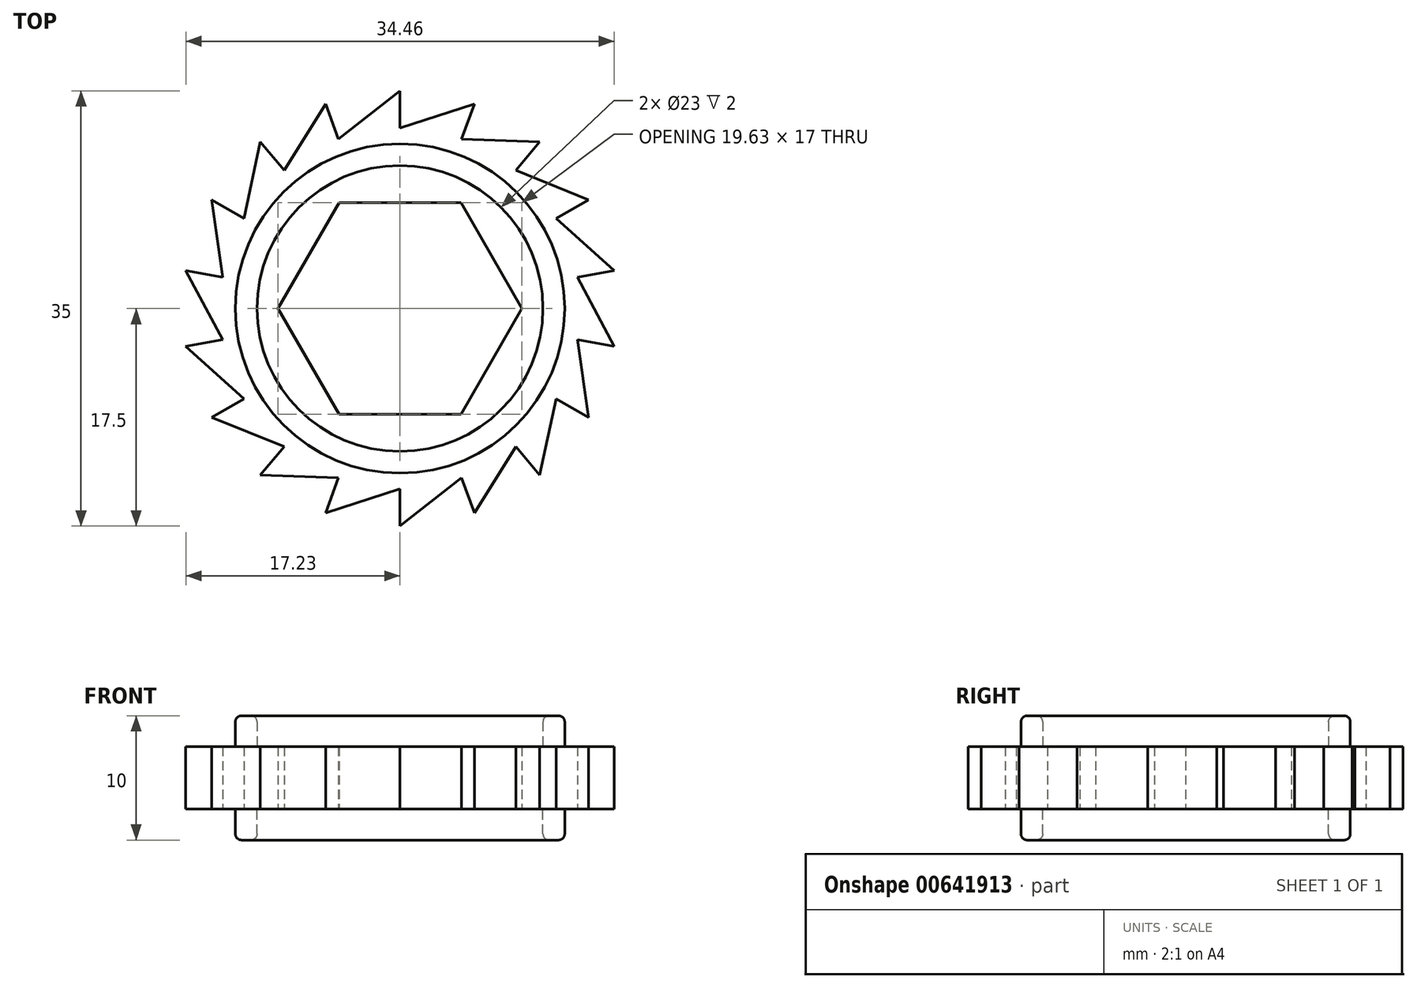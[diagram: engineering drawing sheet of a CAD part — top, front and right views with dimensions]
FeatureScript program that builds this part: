
annotation { "Feature Type Name" : "Feature", "Feature Type Description" : "" }
export const myFeature = defineFeature(function(context is Context, id is Id, definition is map)
    precondition{}
    {
        {
            var Q0;
            Q0=qCreatedBy(makeId("Top.planeOp"),FACE);
            var sketch = newSketch(context, id + "F0", { "sketchPlane" : qUnion([Q0])});
            skCircle(sketch, "E0", {"center": v(0, 0) * mm, "radius": 14.5 * mm});
            skCircle(sketch, "E1", {"center": v(0, 0) * mm, "radius": 17.5 * mm});
            skLineSegment(sketch, "E2", {"start": v(0, 0) * mm, "end": v(0, 17.5) * mm});
            skLineSegment(sketch, "E3.1.0", {"start": v(0, 0) * mm, "end": v(-5.99, 16.44) * mm});
            skLineSegment(sketch, "E3.2.0", {"start": v(0, 0) * mm, "end": v(-11.25, 13.4) * mm});
            skLineSegment(sketch, "E3.3.0", {"start": v(0, 0) * mm, "end": v(-15.16, 8.75) * mm});
            skLineSegment(sketch, "E3.4.0", {"start": v(0, 0) * mm, "end": v(-17.23, 3.04) * mm});
            skLineSegment(sketch, "E3.5.0", {"start": v(0, 0) * mm, "end": v(-17.23, -3.04) * mm});
            skLineSegment(sketch, "E3.6.0", {"start": v(0, 0) * mm, "end": v(-15.16, -8.75) * mm});
            skLineSegment(sketch, "E3.7.0", {"start": v(0, 0) * mm, "end": v(-11.25, -13.4) * mm});
            skLineSegment(sketch, "E3.8.0", {"start": v(0, 0) * mm, "end": v(-5.99, -16.44) * mm});
            skLineSegment(sketch, "E3.9.0", {"start": v(0, 0) * mm, "end": v(0, -17.5) * mm});
            skLineSegment(sketch, "E3.10.0", {"start": v(0, 0) * mm, "end": v(5.99, -16.44) * mm});
            skLineSegment(sketch, "E3.11.0", {"start": v(0, 0) * mm, "end": v(11.25, -13.4) * mm});
            skLineSegment(sketch, "E3.12.0", {"start": v(0, 0) * mm, "end": v(15.16, -8.75) * mm});
            skLineSegment(sketch, "E3.13.0", {"start": v(0, 0) * mm, "end": v(17.23, -3.04) * mm});
            skLineSegment(sketch, "E3.14.0", {"start": v(0, 0) * mm, "end": v(17.23, 3.04) * mm});
            skLineSegment(sketch, "E3.15.0", {"start": v(0, 0) * mm, "end": v(15.16, 8.75) * mm});
            skLineSegment(sketch, "E3.16.0", {"start": v(0, 0) * mm, "end": v(11.25, 13.4) * mm});
            skLineSegment(sketch, "E3.17.0", {"start": v(0, 0) * mm, "end": v(5.99, 16.44) * mm});
            skLineSegment(sketch, "E4", {"start": v(5.99, 16.44) * mm, "end": v(0, 14.5) * mm});
            skLineSegment(sketch, "E5.1.0", {"start": v(0, 17.5) * mm, "end": v(-4.96, 13.63) * mm});
            skLineSegment(sketch, "E5.2.0", {"start": v(-5.99, 16.44) * mm, "end": v(-9.32, 11.1) * mm});
            skLineSegment(sketch, "E5.3.0", {"start": v(-11.25, 13.4) * mm, "end": v(-12.56, 7.25) * mm});
            skLineSegment(sketch, "E5.4.0", {"start": v(-15.16, 8.75) * mm, "end": v(-14.28, 2.52) * mm});
            skLineSegment(sketch, "E5.5.0", {"start": v(-17.23, 3.04) * mm, "end": v(-14.28, -2.52) * mm});
            skLineSegment(sketch, "E5.6.0", {"start": v(-17.23, -3.04) * mm, "end": v(-12.56, -7.25) * mm});
            skLineSegment(sketch, "E5.7.0", {"start": v(-15.16, -8.75) * mm, "end": v(-9.32, -11.1) * mm});
            skLineSegment(sketch, "E5.8.0", {"start": v(-11.25, -13.4) * mm, "end": v(-4.96, -13.63) * mm});
            skLineSegment(sketch, "E5.9.0", {"start": v(-5.99, -16.44) * mm, "end": v(0, -14.5) * mm});
            skLineSegment(sketch, "E5.10.0", {"start": v(0, -17.5) * mm, "end": v(4.96, -13.63) * mm});
            skLineSegment(sketch, "E5.11.0", {"start": v(5.99, -16.44) * mm, "end": v(9.32, -11.1) * mm});
            skLineSegment(sketch, "E5.12.0", {"start": v(11.25, -13.4) * mm, "end": v(12.56, -7.25) * mm});
            skLineSegment(sketch, "E5.13.0", {"start": v(15.16, -8.75) * mm, "end": v(14.28, -2.52) * mm});
            skLineSegment(sketch, "E5.14.0", {"start": v(17.23, -3.04) * mm, "end": v(14.28, 2.52) * mm});
            skLineSegment(sketch, "E5.15.0", {"start": v(17.23, 3.04) * mm, "end": v(12.56, 7.25) * mm});
            skLineSegment(sketch, "E5.16.0", {"start": v(15.16, 8.75) * mm, "end": v(9.32, 11.1) * mm});
            skLineSegment(sketch, "E5.17.0", {"start": v(11.25, 13.4) * mm, "end": v(4.96, 13.63) * mm});
            skCircle(sketch, "E6.cCircle", {"center": v(0, 0) * mm, "radius": 8.5 * mm, "construction": true});
            skLineSegment(sketch, "E6.0", {"start": v(4.9, 8.5) * mm, "end": v(9.81, 0) * mm});
            skLineSegment(sketch, "E6.1", {"start": v(9.81, 0) * mm, "end": v(4.9, -8.5) * mm});
            skLineSegment(sketch, "E6.2", {"start": v(4.9, -8.5) * mm, "end": v(-4.9, -8.5) * mm});
            skLineSegment(sketch, "E6.3", {"start": v(-4.9, -8.5) * mm, "end": v(-9.81, 0) * mm});
            skLineSegment(sketch, "E6.4", {"start": v(-9.81, 0) * mm, "end": v(-4.9, 8.5) * mm});
            skLineSegment(sketch, "E6.5", {"start": v(-4.9, 8.5) * mm, "end": v(4.9, 8.5) * mm});
            skPoint(sketch, "E6.0.midPoint", {"position": v(7.36, 4.25) * mm});
            skSolve(sketch);
        }
        {
            var Q0;
            {var subQ1=sQuery(id+"F0.wireOp",EDGE,"E0");var subQ3=sQuery(id+"F0.wireOp",EDGE,"E3.17.0");var subQ4=makeQuery(id+"F0.imprint","INTERSECT",VERTEX,{"derivedFrom":[subQ1,subQ3]});Q0=makeQuery(id+"F0.imprint","IMPRINT",FACE,{"disambiguationData":[TD([[makeQuery(id+"F0.imprint","IMPRINT",EDGE,{"disambiguationData":[TD([[subQ4,-1.0]])],"derivedFrom":subQ1}),1.0]])]});}
            var Q1;
            {var subQ0=sQuery(id+"F0.wireOp",EDGE,"E4");Q1=makeQuery(id+"F0.imprint","IMPRINT",FACE,{"disambiguationData":[TD([[makeQuery(id+"F0.imprint","IMPRINT",EDGE,{"derivedFrom":subQ0}),1.0]])]});}
            var Q2;
            {var subQ0=sQuery(id+"F0.wireOp",EDGE,"E2");var subQ1=sQuery(id+"F0.wireOp",EDGE,"E0");var subQ2=makeQuery(id+"F0.imprint","INTERSECT",VERTEX,{"derivedFrom":[subQ1,subQ0,sQuery(id+"F0.wireOp",EDGE,"E4")]});Q2=makeQuery(id+"F0.imprint","IMPRINT",FACE,{"disambiguationData":[TD([[makeQuery(id+"F0.imprint","IMPRINT",EDGE,{"disambiguationData":[TD([[subQ2,-1.0]])],"derivedFrom":subQ1}),1.0]])]});}
            var Q3;
            {var subQ3=sQuery(id+"F0.wireOp",EDGE,"E5.1.0");Q3=makeQuery(id+"F0.imprint","IMPRINT",FACE,{"disambiguationData":[TD([[makeQuery(id+"F0.imprint","IMPRINT",EDGE,{"derivedFrom":subQ3}),1.0]])]});}
            var Q4;
            {var subQ0=sQuery(id+"F0.wireOp",EDGE,"E3.16.0");var subQ1=sQuery(id+"F0.wireOp",EDGE,"E0");var subQ2=makeQuery(id+"F0.imprint","INTERSECT",VERTEX,{"derivedFrom":[subQ1,subQ0,sQuery(id+"F0.wireOp",EDGE,"E5.16.0")]});Q4=makeQuery(id+"F0.imprint","IMPRINT",FACE,{"disambiguationData":[TD([[makeQuery(id+"F0.imprint","IMPRINT",EDGE,{"disambiguationData":[TD([[subQ2,-1.0]])],"derivedFrom":subQ1}),1.0]])]});}
            var Q5;
            {var subQ3=sQuery(id+"F0.wireOp",EDGE,"E5.17.0");Q5=makeQuery(id+"F0.imprint","IMPRINT",FACE,{"disambiguationData":[TD([[makeQuery(id+"F0.imprint","IMPRINT",EDGE,{"derivedFrom":subQ3}),1.0]])]});}
            var Q6;
            {var subQ3=sQuery(id+"F0.wireOp",EDGE,"E5.16.0");Q6=makeQuery(id+"F0.imprint","IMPRINT",FACE,{"disambiguationData":[TD([[makeQuery(id+"F0.imprint","IMPRINT",EDGE,{"derivedFrom":subQ3}),1.0]])]});}
            var Q7;
            {var subQ0=sQuery(id+"F0.wireOp",EDGE,"E3.14.0");var subQ1=sQuery(id+"F0.wireOp",EDGE,"E0");var subQ2=makeQuery(id+"F0.imprint","INTERSECT",VERTEX,{"derivedFrom":[subQ1,subQ0,sQuery(id+"F0.wireOp",EDGE,"E5.14.0")]});Q7=makeQuery(id+"F0.imprint","IMPRINT",FACE,{"disambiguationData":[TD([[makeQuery(id+"F0.imprint","IMPRINT",EDGE,{"disambiguationData":[TD([[subQ2,-1.0]])],"derivedFrom":subQ1}),1.0]])]});}
            var Q8;
            {var subQ3=sQuery(id+"F0.wireOp",EDGE,"E5.15.0");Q8=makeQuery(id+"F0.imprint","IMPRINT",FACE,{"disambiguationData":[TD([[makeQuery(id+"F0.imprint","IMPRINT",EDGE,{"derivedFrom":subQ3}),1.0]])]});}
            var Q9;
            {var subQ0=sQuery(id+"F0.wireOp",EDGE,"E3.13.0");var subQ1=sQuery(id+"F0.wireOp",EDGE,"E0");var subQ2=makeQuery(id+"F0.imprint","INTERSECT",VERTEX,{"derivedFrom":[subQ1,subQ0,sQuery(id+"F0.wireOp",EDGE,"E5.13.0")]});Q9=makeQuery(id+"F0.imprint","IMPRINT",FACE,{"disambiguationData":[TD([[makeQuery(id+"F0.imprint","IMPRINT",EDGE,{"disambiguationData":[TD([[subQ2,-1.0]])],"derivedFrom":subQ1}),1.0]])]});}
            var Q10;
            {var subQ3=sQuery(id+"F0.wireOp",EDGE,"E5.14.0");Q10=makeQuery(id+"F0.imprint","IMPRINT",FACE,{"disambiguationData":[TD([[makeQuery(id+"F0.imprint","IMPRINT",EDGE,{"derivedFrom":subQ3}),1.0]])]});}
            var Q11;
            {var subQ0=sQuery(id+"F0.wireOp",EDGE,"E3.12.0");var subQ1=sQuery(id+"F0.wireOp",EDGE,"E0");var subQ2=makeQuery(id+"F0.imprint","INTERSECT",VERTEX,{"derivedFrom":[subQ1,subQ0,sQuery(id+"F0.wireOp",EDGE,"E5.12.0")]});Q11=makeQuery(id+"F0.imprint","IMPRINT",FACE,{"disambiguationData":[TD([[makeQuery(id+"F0.imprint","IMPRINT",EDGE,{"disambiguationData":[TD([[subQ2,-1.0]])],"derivedFrom":subQ1}),1.0]])]});}
            var Q12;
            {var subQ3=sQuery(id+"F0.wireOp",EDGE,"E5.13.0");Q12=makeQuery(id+"F0.imprint","IMPRINT",FACE,{"disambiguationData":[TD([[makeQuery(id+"F0.imprint","IMPRINT",EDGE,{"derivedFrom":subQ3}),1.0]])]});}
            var Q13;
            {var subQ0=sQuery(id+"F0.wireOp",EDGE,"E3.11.0");var subQ1=sQuery(id+"F0.wireOp",EDGE,"E0");var subQ2=makeQuery(id+"F0.imprint","INTERSECT",VERTEX,{"derivedFrom":[subQ1,subQ0,sQuery(id+"F0.wireOp",EDGE,"E5.11.0")]});Q13=makeQuery(id+"F0.imprint","IMPRINT",FACE,{"disambiguationData":[TD([[makeQuery(id+"F0.imprint","IMPRINT",EDGE,{"disambiguationData":[TD([[subQ2,-1.0]])],"derivedFrom":subQ1}),1.0]])]});}
            var Q14;
            {var subQ3=sQuery(id+"F0.wireOp",EDGE,"E5.12.0");Q14=makeQuery(id+"F0.imprint","IMPRINT",FACE,{"disambiguationData":[TD([[makeQuery(id+"F0.imprint","IMPRINT",EDGE,{"derivedFrom":subQ3}),1.0]])]});}
            var Q15;
            {var subQ0=sQuery(id+"F0.wireOp",EDGE,"E3.10.0");var subQ1=sQuery(id+"F0.wireOp",EDGE,"E0");var subQ2=makeQuery(id+"F0.imprint","INTERSECT",VERTEX,{"derivedFrom":[subQ1,subQ0,sQuery(id+"F0.wireOp",EDGE,"E5.10.0")]});Q15=makeQuery(id+"F0.imprint","IMPRINT",FACE,{"disambiguationData":[TD([[makeQuery(id+"F0.imprint","IMPRINT",EDGE,{"disambiguationData":[TD([[subQ2,-1.0]])],"derivedFrom":subQ1}),1.0]])]});}
            var Q16;
            {var subQ3=sQuery(id+"F0.wireOp",EDGE,"E5.11.0");Q16=makeQuery(id+"F0.imprint","IMPRINT",FACE,{"disambiguationData":[TD([[makeQuery(id+"F0.imprint","IMPRINT",EDGE,{"derivedFrom":subQ3}),1.0]])]});}
            var Q17;
            {var subQ3=sQuery(id+"F0.wireOp",EDGE,"E5.10.0");Q17=makeQuery(id+"F0.imprint","IMPRINT",FACE,{"disambiguationData":[TD([[makeQuery(id+"F0.imprint","IMPRINT",EDGE,{"derivedFrom":subQ3}),1.0]])]});}
            var Q18;
            {var subQ0=sQuery(id+"F0.wireOp",EDGE,"E3.8.0");var subQ1=sQuery(id+"F0.wireOp",EDGE,"E0");var subQ2=makeQuery(id+"F0.imprint","INTERSECT",VERTEX,{"derivedFrom":[subQ1,subQ0,sQuery(id+"F0.wireOp",EDGE,"E5.8.0")]});Q18=makeQuery(id+"F0.imprint","IMPRINT",FACE,{"disambiguationData":[TD([[makeQuery(id+"F0.imprint","IMPRINT",EDGE,{"disambiguationData":[TD([[subQ2,-1.0]])],"derivedFrom":subQ1}),1.0]])]});}
            var Q19;
            {var subQ3=sQuery(id+"F0.wireOp",EDGE,"E5.9.0");Q19=makeQuery(id+"F0.imprint","IMPRINT",FACE,{"disambiguationData":[TD([[makeQuery(id+"F0.imprint","IMPRINT",EDGE,{"derivedFrom":subQ3}),1.0]])]});}
            var Q20;
            {var subQ0=sQuery(id+"F0.wireOp",EDGE,"E3.15.0");var subQ1=sQuery(id+"F0.wireOp",EDGE,"E0");var subQ2=makeQuery(id+"F0.imprint","INTERSECT",VERTEX,{"derivedFrom":[subQ1,subQ0,sQuery(id+"F0.wireOp",EDGE,"E5.15.0")]});Q20=makeQuery(id+"F0.imprint","IMPRINT",FACE,{"disambiguationData":[TD([[makeQuery(id+"F0.imprint","IMPRINT",EDGE,{"disambiguationData":[TD([[subQ2,-1.0]])],"derivedFrom":subQ1}),1.0]])]});}
            var Q21;
            {var subQ0=sQuery(id+"F0.wireOp",EDGE,"E3.9.0");var subQ1=sQuery(id+"F0.wireOp",EDGE,"E0");var subQ2=makeQuery(id+"F0.imprint","INTERSECT",VERTEX,{"derivedFrom":[subQ1,subQ0,sQuery(id+"F0.wireOp",EDGE,"E5.9.0")]});Q21=makeQuery(id+"F0.imprint","IMPRINT",FACE,{"disambiguationData":[TD([[makeQuery(id+"F0.imprint","IMPRINT",EDGE,{"disambiguationData":[TD([[subQ2,-1.0]])],"derivedFrom":subQ1}),1.0]])]});}
            var Q22;
            {var subQ0=sQuery(id+"F0.wireOp",EDGE,"E3.7.0");var subQ1=sQuery(id+"F0.wireOp",EDGE,"E0");var subQ2=makeQuery(id+"F0.imprint","INTERSECT",VERTEX,{"derivedFrom":[subQ1,subQ0,sQuery(id+"F0.wireOp",EDGE,"E5.7.0")]});Q22=makeQuery(id+"F0.imprint","IMPRINT",FACE,{"disambiguationData":[TD([[makeQuery(id+"F0.imprint","IMPRINT",EDGE,{"disambiguationData":[TD([[subQ2,-1.0]])],"derivedFrom":subQ1}),1.0]])]});}
            var Q23;
            {var subQ3=sQuery(id+"F0.wireOp",EDGE,"E5.8.0");Q23=makeQuery(id+"F0.imprint","IMPRINT",FACE,{"disambiguationData":[TD([[makeQuery(id+"F0.imprint","IMPRINT",EDGE,{"derivedFrom":subQ3}),1.0]])]});}
            var Q24;
            {var subQ3=sQuery(id+"F0.wireOp",EDGE,"E5.7.0");Q24=makeQuery(id+"F0.imprint","IMPRINT",FACE,{"disambiguationData":[TD([[makeQuery(id+"F0.imprint","IMPRINT",EDGE,{"derivedFrom":subQ3}),1.0]])]});}
            var Q25;
            {var subQ0=sQuery(id+"F0.wireOp",EDGE,"E3.6.0");var subQ1=sQuery(id+"F0.wireOp",EDGE,"E0");var subQ2=makeQuery(id+"F0.imprint","INTERSECT",VERTEX,{"derivedFrom":[subQ1,subQ0,sQuery(id+"F0.wireOp",EDGE,"E5.6.0")]});Q25=makeQuery(id+"F0.imprint","IMPRINT",FACE,{"disambiguationData":[TD([[makeQuery(id+"F0.imprint","IMPRINT",EDGE,{"disambiguationData":[TD([[subQ2,-1.0]])],"derivedFrom":subQ1}),1.0]])]});}
            var Q26;
            {var subQ3=sQuery(id+"F0.wireOp",EDGE,"E5.6.0");Q26=makeQuery(id+"F0.imprint","IMPRINT",FACE,{"disambiguationData":[TD([[makeQuery(id+"F0.imprint","IMPRINT",EDGE,{"derivedFrom":subQ3}),1.0]])]});}
            var Q27;
            {var subQ0=sQuery(id+"F0.wireOp",EDGE,"E3.5.0");var subQ1=sQuery(id+"F0.wireOp",EDGE,"E0");var subQ2=makeQuery(id+"F0.imprint","INTERSECT",VERTEX,{"derivedFrom":[subQ1,subQ0,sQuery(id+"F0.wireOp",EDGE,"E5.5.0")]});Q27=makeQuery(id+"F0.imprint","IMPRINT",FACE,{"disambiguationData":[TD([[makeQuery(id+"F0.imprint","IMPRINT",EDGE,{"disambiguationData":[TD([[subQ2,-1.0]])],"derivedFrom":subQ1}),1.0]])]});}
            var Q28;
            {var subQ3=sQuery(id+"F0.wireOp",EDGE,"E5.5.0");Q28=makeQuery(id+"F0.imprint","IMPRINT",FACE,{"disambiguationData":[TD([[makeQuery(id+"F0.imprint","IMPRINT",EDGE,{"derivedFrom":subQ3}),1.0]])]});}
            var Q29;
            {var subQ0=sQuery(id+"F0.wireOp",EDGE,"E3.4.0");var subQ1=sQuery(id+"F0.wireOp",EDGE,"E0");var subQ2=makeQuery(id+"F0.imprint","INTERSECT",VERTEX,{"derivedFrom":[subQ1,subQ0,sQuery(id+"F0.wireOp",EDGE,"E5.4.0")]});Q29=makeQuery(id+"F0.imprint","IMPRINT",FACE,{"disambiguationData":[TD([[makeQuery(id+"F0.imprint","IMPRINT",EDGE,{"disambiguationData":[TD([[subQ2,-1.0]])],"derivedFrom":subQ1}),1.0]])]});}
            var Q30;
            {var subQ3=sQuery(id+"F0.wireOp",EDGE,"E5.4.0");Q30=makeQuery(id+"F0.imprint","IMPRINT",FACE,{"disambiguationData":[TD([[makeQuery(id+"F0.imprint","IMPRINT",EDGE,{"derivedFrom":subQ3}),1.0]])]});}
            var Q31;
            {var subQ0=sQuery(id+"F0.wireOp",EDGE,"E3.3.0");var subQ1=sQuery(id+"F0.wireOp",EDGE,"E0");var subQ2=makeQuery(id+"F0.imprint","INTERSECT",VERTEX,{"derivedFrom":[subQ1,subQ0,sQuery(id+"F0.wireOp",EDGE,"E5.3.0")]});Q31=makeQuery(id+"F0.imprint","IMPRINT",FACE,{"disambiguationData":[TD([[makeQuery(id+"F0.imprint","IMPRINT",EDGE,{"disambiguationData":[TD([[subQ2,-1.0]])],"derivedFrom":subQ1}),1.0]])]});}
            var Q32;
            {var subQ3=sQuery(id+"F0.wireOp",EDGE,"E5.3.0");Q32=makeQuery(id+"F0.imprint","IMPRINT",FACE,{"disambiguationData":[TD([[makeQuery(id+"F0.imprint","IMPRINT",EDGE,{"derivedFrom":subQ3}),1.0]])]});}
            var Q33;
            {var subQ0=sQuery(id+"F0.wireOp",EDGE,"E3.2.0");var subQ1=sQuery(id+"F0.wireOp",EDGE,"E0");var subQ2=makeQuery(id+"F0.imprint","INTERSECT",VERTEX,{"derivedFrom":[subQ1,subQ0,sQuery(id+"F0.wireOp",EDGE,"E5.2.0")]});Q33=makeQuery(id+"F0.imprint","IMPRINT",FACE,{"disambiguationData":[TD([[makeQuery(id+"F0.imprint","IMPRINT",EDGE,{"disambiguationData":[TD([[subQ2,-1.0]])],"derivedFrom":subQ1}),1.0]])]});}
            var Q34;
            {var subQ3=sQuery(id+"F0.wireOp",EDGE,"E5.2.0");Q34=makeQuery(id+"F0.imprint","IMPRINT",FACE,{"disambiguationData":[TD([[makeQuery(id+"F0.imprint","IMPRINT",EDGE,{"derivedFrom":subQ3}),1.0]])]});}
            var Q35;
            {var subQ0=sQuery(id+"F0.wireOp",EDGE,"E3.1.0");var subQ1=sQuery(id+"F0.wireOp",EDGE,"E0");var subQ2=makeQuery(id+"F0.imprint","INTERSECT",VERTEX,{"derivedFrom":[subQ1,subQ0,sQuery(id+"F0.wireOp",EDGE,"E5.1.0")]});Q35=makeQuery(id+"F0.imprint","IMPRINT",FACE,{"disambiguationData":[TD([[makeQuery(id+"F0.imprint","IMPRINT",EDGE,{"disambiguationData":[TD([[subQ2,-1.0]])],"derivedFrom":subQ1}),1.0]])]});}
            extrude(context, id + "F1", {"entities" : qUnion([Q0, Q1, Q2, Q3, Q4, Q5, Q6, Q7, Q8, Q9, Q10, Q11, Q12, Q13, Q14, Q15, Q16, Q17, Q18, Q19, Q20, Q21, Q22, Q23, Q24, Q25, Q26, Q27, Q28, Q29, Q30, Q31, Q32, Q33, Q34, Q35]), "depth" : 5 * mm, "offsetDistance" : 25 * mm});
        }
        {
            var Q0;
            Q0=makeQuery(id+"F1.opExtrude","CAP_FACE",FACE,{"disambiguationData":[OSD([sQuery(id+"F0.wireOp",EDGE,"E2"),sQuery(id+"F0.wireOp",EDGE,"E3.1.0"),sQuery(id+"F0.wireOp",EDGE,"E3.2.0"),sQuery(id+"F0.wireOp",EDGE,"E3.3.0"),sQuery(id+"F0.wireOp",EDGE,"E3.4.0"),sQuery(id+"F0.wireOp",EDGE,"E3.5.0"),sQuery(id+"F0.wireOp",EDGE,"E3.6.0"),sQuery(id+"F0.wireOp",EDGE,"E3.7.0"),sQuery(id+"F0.wireOp",EDGE,"E3.8.0"),sQuery(id+"F0.wireOp",EDGE,"E3.9.0"),sQuery(id+"F0.wireOp",EDGE,"E3.10.0"),sQuery(id+"F0.wireOp",EDGE,"E3.11.0"),sQuery(id+"F0.wireOp",EDGE,"E3.12.0"),sQuery(id+"F0.wireOp",EDGE,"E3.13.0"),sQuery(id+"F0.wireOp",EDGE,"E3.14.0"),sQuery(id+"F0.wireOp",EDGE,"E3.15.0"),sQuery(id+"F0.wireOp",EDGE,"E3.16.0"),sQuery(id+"F0.wireOp",EDGE,"E3.17.0"),sQuery(id+"F0.wireOp",EDGE,"E4"),sQuery(id+"F0.wireOp",EDGE,"E5.1.0"),sQuery(id+"F0.wireOp",EDGE,"E5.2.0"),sQuery(id+"F0.wireOp",EDGE,"E5.3.0"),sQuery(id+"F0.wireOp",EDGE,"E5.4.0"),sQuery(id+"F0.wireOp",EDGE,"E5.5.0"),sQuery(id+"F0.wireOp",EDGE,"E5.6.0"),sQuery(id+"F0.wireOp",EDGE,"E5.7.0"),sQuery(id+"F0.wireOp",EDGE,"E5.8.0"),sQuery(id+"F0.wireOp",EDGE,"E5.9.0"),sQuery(id+"F0.wireOp",EDGE,"E5.10.0"),sQuery(id+"F0.wireOp",EDGE,"E5.11.0"),sQuery(id+"F0.wireOp",EDGE,"E5.12.0"),sQuery(id+"F0.wireOp",EDGE,"E5.13.0"),sQuery(id+"F0.wireOp",EDGE,"E5.14.0"),sQuery(id+"F0.wireOp",EDGE,"E5.15.0"),sQuery(id+"F0.wireOp",EDGE,"E5.16.0"),sQuery(id+"F0.wireOp",EDGE,"E5.17.0"),sQuery(id+"F0.wireOp",EDGE,"E6.0"),sQuery(id+"F0.wireOp",EDGE,"E6.1"),sQuery(id+"F0.wireOp",EDGE,"E6.2"),sQuery(id+"F0.wireOp",EDGE,"E6.3"),sQuery(id+"F0.wireOp",EDGE,"E6.4"),sQuery(id+"F0.wireOp",EDGE,"E6.5")])],"isStart":false});
            var sketch = newSketch(context, id + "F2", { "sketchPlane" : qUnion([Q0])});
            skCircle(sketch, "E7", {"center": v(0, 0) * mm, "radius": 13.25 * mm});
            skCircle(sketch, "E8", {"center": v(0, 0) * mm, "radius": 11.5 * mm});
            skSolve(sketch);
        }
        {
            var Q0;
            Q0=makeQuery(id+"F2.imprint","IMPRINT",FACE,{"disambiguationData":[TD([[makeQuery(id+"F2.imprint","IMPRINT",EDGE,{"derivedFrom":sQuery(id+"F2.wireOp",EDGE,"E7")}),1.0]])]});
            extrude(context, id + "F3", {"entities" : qUnion([Q0]), "operationType" : NewBodyOperationType.ADD, "depth" : 2.5 * mm, "offsetDistance" : 25 * mm});
        }
        {
            var Q0;
            {var subQ3=sQuery(id+"F0.wireOp",EDGE,"E6.4");var subQ5=sQuery(id+"F0.wireOp",EDGE,"E6.3");var subQ6=makeQuery(id+"F0.imprint","INTERSECT",VERTEX,{"derivedFrom":[subQ5,subQ3]});Q0=makeQuery(id+"F0.imprint","IMPRINT",FACE,{"disambiguationData":[TD([[makeQuery(id+"F0.imprint","IMPRINT",EDGE,{"disambiguationData":[TD([[subQ6,1.0]])],"derivedFrom":subQ5}),-1.0]])]});}
            var sketch = newSketch(context, id + "F4", { "sketchPlane" : qUnion([Q0])});
            skCircle(sketch, "E9", {"center": v(0, 0) * mm, "radius": 11.5 * mm});
            skCircle(sketch, "E10", {"center": v(0, 0) * mm, "radius": 13.25 * mm});
            skSolve(sketch);
        }
        {
            var Q0;
            Q0=makeQuery(id+"F4.imprint","IMPRINT",FACE,{"disambiguationData":[TD([[makeQuery(id+"F4.imprint","IMPRINT",EDGE,{"derivedFrom":sQuery(id+"F4.wireOp",EDGE,"E9")}),-1.0]])]});
            extrude(context, id + "F5", {"entities" : qUnion([Q0]), "operationType" : NewBodyOperationType.ADD, "oppositeDirection" : true, "depth" : 2.5 * mm, "offsetDistance" : 25 * mm});
        }
        {
            var Q0;
            Q0=makeQuery(id+"F3.opExtrude","CAP_EDGE",EDGE,{"disambiguationData":[OSD([sQuery(id+"F2.wireOp",EDGE,"E7")])],"isStart":false});
            var Q1;
            Q1=makeQuery(id+"F3.opExtrude","CAP_EDGE",EDGE,{"disambiguationData":[OSD([sQuery(id+"F2.wireOp",EDGE,"E8")])],"isStart":false});
            var Q2;
            Q2=makeQuery(id+"F5.opExtrude","CAP_EDGE",EDGE,{"disambiguationData":[OSD([sQuery(id+"F4.wireOp",EDGE,"E10")])],"isStart":false});
            var Q3;
            Q3=makeQuery(id+"F5.opExtrude","CAP_EDGE",EDGE,{"disambiguationData":[OSD([sQuery(id+"F4.wireOp",EDGE,"E9")])],"isStart":false});
            fillet(context, id + "F6", {"entities" : qUnion([Q0, Q1, Q2, Q3]), "radius" : 0.5 * mm, "tangentPropagation" : true, "allowEdgeOverflow" : false});
        }
    });
